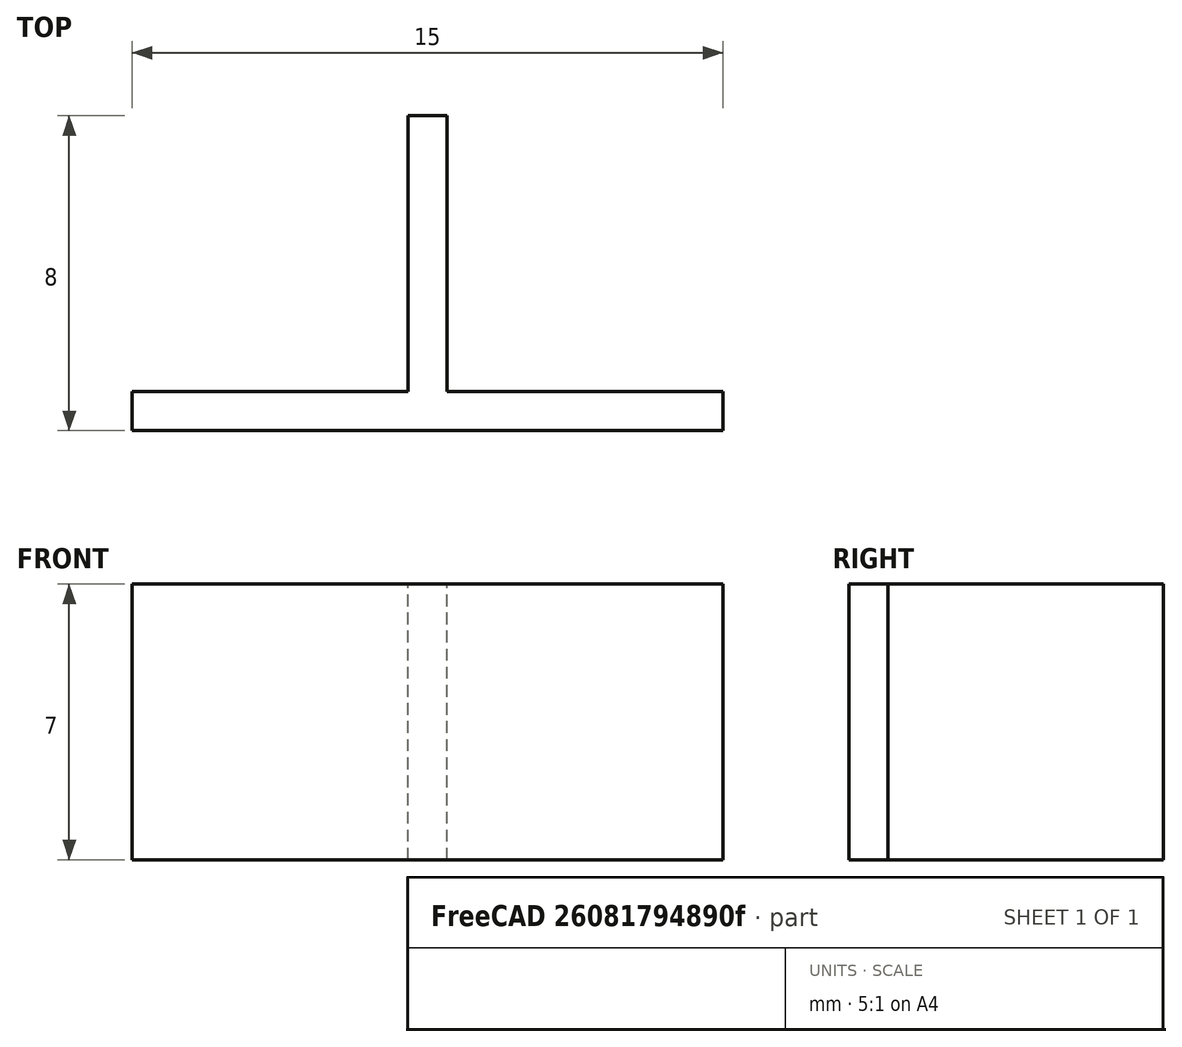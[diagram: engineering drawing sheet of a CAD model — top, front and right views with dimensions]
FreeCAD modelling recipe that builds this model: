
FCSTD DOCUMENT  (FreeCAD 0.18R16146 (Git))
Label: enstop_switch
License: All rights reserved
LicenseURL: http://en.wikipedia.org/wiki/All_rights_reserved
objects: Sketcher::SketchObject×1, PartDesign::Pad×1, PartDesign::Body×1
note: 4 computed .brp shape members not serialized (recipe doc carries the construction recipe); baked Part::Feature solids carry a one-line shape summary decoded from their .brp

FEATURE [Sketcher::SketchObject] Sketch
  MapMode = 5
  Support = -> [XY_Plane]
  sketch-geometry (8):
    g0: LineSegment StartX=0 StartY=0 StartZ=0 EndX=15 EndY=0 EndZ=0
    g1: LineSegment StartX=15 StartY=0 StartZ=0 EndX=15 EndY=1 EndZ=0
    g2: LineSegment StartX=15 StartY=1 StartZ=0 EndX=8 EndY=1 EndZ=0
    g3: LineSegment StartX=8 StartY=1 StartZ=0 EndX=8 EndY=8 EndZ=0
    g4: LineSegment StartX=8 StartY=8 StartZ=0 EndX=7 EndY=8 EndZ=0
    g5: LineSegment StartX=7 StartY=8 StartZ=0 EndX=7 EndY=1 EndZ=0
    g6: LineSegment StartX=7 StartY=1 StartZ=0 EndX=0 EndY=1 EndZ=0
    g7: LineSegment StartX=0 StartY=1 StartZ=0 EndX=0 EndY=0 EndZ=0
  constraints (23):
    c: Coincident(g0,g1)
    c: Coincident(g1,g2)
    c: Coincident(g2,g3)
    c: Coincident(g3,g4)
    c: Coincident(g4,g5)
    c: Coincident(g5,g6)
    c: Coincident(g6,g7)
    c: Coincident(g0,g7)
    c: Coincident(g0,g-1)
    c: Horizontal(g6)
    c: Horizontal(g0)
    c: Horizontal(g2)
    c: Vertical(g7)
    c: Vertical(g5)
    c: Vertical(g3)
    c: Vertical(g1)
    c: Equal(g7,g1)
    c: Equal(g1,g4)
    c: Equal(g6,g2)
    c: Equal(g2,g5)
    c: Equal(g5,g3)
    c: DistanceX(g6,g6) = 7
    c: DistanceY(g7,g7) = 1
FEATURE [PartDesign::Pad] Pad
  Length = 7
  Length2 = 100
  Profile = -> Sketch
  Type = 0
FEATURE [PartDesign::Body] Body
  Group = -> [Sketch,Pad]
  Origin = -> Origin
  Tip = -> Pad
